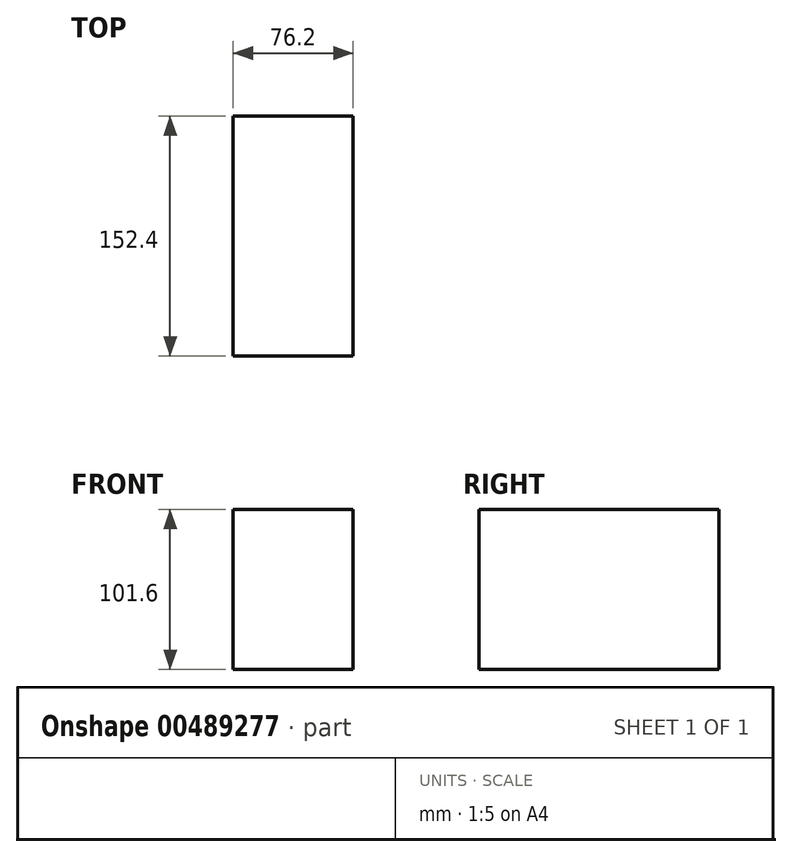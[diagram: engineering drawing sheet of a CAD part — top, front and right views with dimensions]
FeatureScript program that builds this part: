
annotation { "Feature Type Name" : "Feature", "Feature Type Description" : "" }
export const myFeature = defineFeature(function(context is Context, id is Id, definition is map)
    precondition{}
    {
        {
            var Q0;
            Q0=qCreatedBy(makeId("Front.planeOp"),FACE);
            var sketch = newSketch(context, id + "F0", { "sketchPlane" : qUnion([Q0])});
            skLineSegment(sketch, "E0.bottom", {"start": v(31.88, 46) * mm, "end": v(108.08, 46) * mm});
            skLineSegment(sketch, "E0.top", {"start": v(31.88, 147.6) * mm, "end": v(108.08, 147.6) * mm});
            skLineSegment(sketch, "E0.left", {"start": v(31.88, 46) * mm, "end": v(31.88, 147.6) * mm});
            skLineSegment(sketch, "E0.right", {"start": v(108.08, 46) * mm, "end": v(108.08, 147.6) * mm});
            skSolve(sketch);
        }
        {
            var Q0;
            Q0=makeQuery(id+"F0.imprint","IMPRINT",FACE,{"disambiguationData":[TD([[makeQuery(id+"F0.imprint","IMPRINT",EDGE,{"derivedFrom":sQuery(id+"F0.wireOp",EDGE,"E0.bottom")}),1.0]])]});
            extrude(context, id + "F1", {"entities" : qUnion([Q0]), "endBound" : BoundingType.SYMMETRIC, "depth" : 152.4 * mm});
        }
        {
            var Q0;
            Q0=makeQuery(id+"F1.opExtrude","SWEPT_FACE",FACE,{"disambiguationData":[OSD([sQuery(id+"F0.wireOp",EDGE,"E0.top")])]});
            var sketch = newSketch(context, id + "F2", { "sketchPlane" : qUnion([Q0])});
            skCircle(sketch, "E1", {"center": v(53.65, 18.88) * mm, "radius": 35.41 * mm});
            skSolve(sketch);
        }
        {
            var Q0;
            Q0=sQuery(id+"F2.wireOp",EDGE,"E1");
            var Q1;
            Q1=makeQuery(id+"F1.opExtrude","CAP_EDGE",EDGE,{"disambiguationData":[OSD([sQuery(id+"F0.wireOp",EDGE,"E0.top")])],"isStart":true});
            revolve(context, id + "F3", {"bodyType" : ToolBodyType.SURFACE, "surfaceEntities" : qUnion([Q0]), "axis" : qUnion([Q1]), "revolveType" : RevolveType.ONE_DIRECTION, "angle" : 360 * degree});
        }
    });
